# Revit family: QF-Remote_Cartridge-OptiPure-CTO-Q10CR
name_source: partatom
category: Specialty Equipment
revit_build: Autodesk Revit 2017 (Build: 20160225_1515(x64)
units: mm (PartAtom-declared; Revit-internal decimal feet)

## family parameters
Always vertical = Yes
Cut with Voids When Loaded = No
OmniClass Number = 23.40.40.14
OmniClass Title = Food Service Equipment
Part Type = Normal
Room Calculation Point = No
Round Connector Dimension = Use Diameter
Shared = No
Work Plane-Based = No

## types (1)
- CTO-QCR
    Assembly Code = E1090300
    Cold Water Maximum Pressure = 10.00 psi
    Cold Water Minimum Pressure = 125.00 psi
    Description = REMOTE CARTRIDGE
    Filtered Water Flow = 1 GPM
    Filtered Water In = 0"
    Filtered Water Out = 0"
    Height = 15.44 "
    Inlet Water Temperature Range = 35-100°F
    Keynote = 11400
    Length = 3.94 "
    Manufacturer = OPTIPURE
    Material = White Plastic
    Model = CTO-QCR
    URL = WWW.OPTIPUREWATER.COM
    Width = 3.94 "

## geometry (parser evidence)
native form markers: Sweep x3
no freeform markers — native parametric forms only
